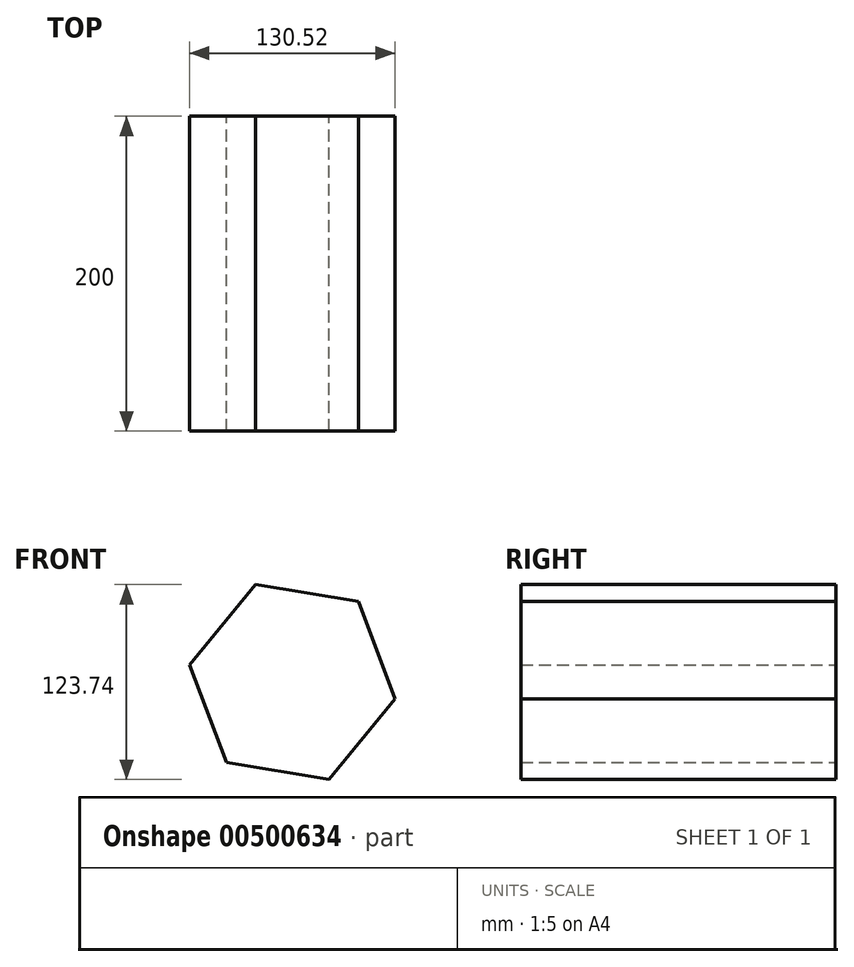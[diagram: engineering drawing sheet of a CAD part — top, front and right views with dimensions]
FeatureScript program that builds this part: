
annotation { "Feature Type Name" : "Feature", "Feature Type Description" : "" }
export const myFeature = defineFeature(function(context is Context, id is Id, definition is map)
    precondition{}
    {
        {
            var Q0;
            Q0=qCreatedBy(makeId("Front.planeOp"),FACE);
            var sketch = newSketch(context, id + "F0", { "sketchPlane" : qUnion([Q0])});
            skCircle(sketch, "E0.cCircle", {"center": v(0, 0) * mm, "radius": 57.27 * mm, "construction": true});
            skLineSegment(sketch, "E0.0", {"start": v(65.26, -10.7) * mm, "end": v(23.35, -61.87) * mm});
            skLineSegment(sketch, "E0.1", {"start": v(23.35, -61.87) * mm, "end": v(-41.9, -51.16) * mm});
            skLineSegment(sketch, "E0.2", {"start": v(-41.9, -51.16) * mm, "end": v(-65.26, 10.7) * mm});
            skLineSegment(sketch, "E0.3", {"start": v(-65.26, 10.7) * mm, "end": v(-23.35, 61.87) * mm});
            skLineSegment(sketch, "E0.4", {"start": v(-23.35, 61.87) * mm, "end": v(41.9, 51.16) * mm});
            skLineSegment(sketch, "E0.5", {"start": v(41.9, 51.16) * mm, "end": v(65.26, -10.7) * mm});
            skPoint(sketch, "E0.0.midPoint", {"position": v(44.3, -36.29) * mm});
            skSolve(sketch);
        }
        {
            var Q0;
            Q0=makeQuery(id+"F0.imprint","IMPRINT",FACE,{"disambiguationData":[TD([[makeQuery(id+"F0.imprint","IMPRINT",EDGE,{"derivedFrom":sQuery(id+"F0.wireOp",EDGE,"E0.0")}),-1.0]])]});
            extrude(context, id + "F1", {"entities" : qUnion([Q0]), "depth" : 200 * mm});
        }
    });
